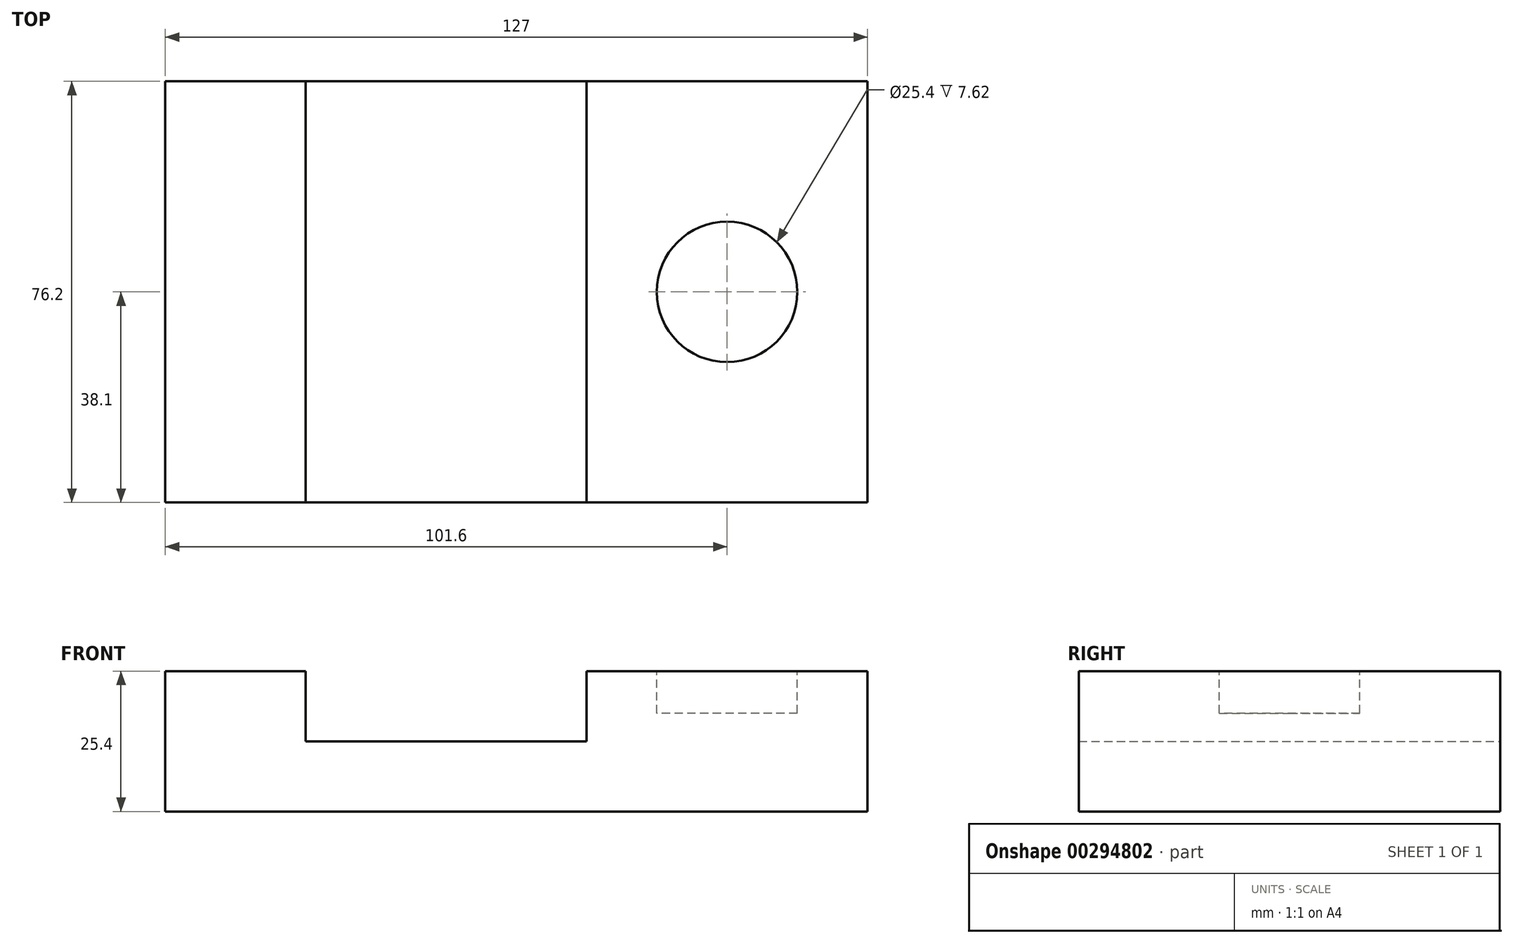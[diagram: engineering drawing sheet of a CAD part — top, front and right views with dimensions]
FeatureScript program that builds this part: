
annotation { "Feature Type Name" : "Feature", "Feature Type Description" : "" }
export const myFeature = defineFeature(function(context is Context, id is Id, definition is map)
    precondition{}
    {
        {
            var Q0;
            Q0=qCreatedBy(makeId("Top.planeOp"),FACE);
            var sketch = newSketch(context, id + "F0", { "sketchPlane" : qUnion([Q0])});
            skLineSegment(sketch, "E0.bottom", {"start": v(0, 0) * mm, "end": v(127, 0) * mm});
            skLineSegment(sketch, "E0.top", {"start": v(0, -76.2) * mm, "end": v(127, -76.2) * mm});
            skLineSegment(sketch, "E0.left", {"start": v(0, 0) * mm, "end": v(0, -76.2) * mm});
            skLineSegment(sketch, "E0.right", {"start": v(127, 0) * mm, "end": v(127, -76.2) * mm});
            skSolve(sketch);
        }
        {
            var Q0;
            Q0=makeQuery(id+"F0.imprint","IMPRINT",FACE,{"disambiguationData":[TD([[makeQuery(id+"F0.imprint","IMPRINT",EDGE,{"derivedFrom":sQuery(id+"F0.wireOp",EDGE,"E0.bottom")}),-1.0]])]});
            extrude(context, id + "F1", {"entities" : qUnion([Q0]), "depth" : 25.4 * mm});
        }
        {
            var Q0;
            Q0=makeQuery(id+"F1.opExtrude","CAP_FACE",FACE,{"disambiguationData":[OSD([sQuery(id+"F0.wireOp",EDGE,"E0.bottom"),sQuery(id+"F0.wireOp",EDGE,"E0.top"),sQuery(id+"F0.wireOp",EDGE,"E0.left"),sQuery(id+"F0.wireOp",EDGE,"E0.right")])],"isStart":false});
            var sketch = newSketch(context, id + "F2", { "sketchPlane" : qUnion([Q0])});
            skLineSegment(sketch, "E1.bottom", {"start": v(25.4, -76.2) * mm, "end": v(76.2, -76.2) * mm});
            skLineSegment(sketch, "E1.top", {"start": v(25.4, 0) * mm, "end": v(76.2, 0) * mm});
            skLineSegment(sketch, "E1.left", {"start": v(25.4, -76.2) * mm, "end": v(25.4, 0) * mm});
            skLineSegment(sketch, "E1.right", {"start": v(76.2, -76.2) * mm, "end": v(76.2, 0) * mm});
            skSolve(sketch);
        }
        {
            var Q0;
            Q0=makeQuery(id+"F2.imprint","IMPRINT",FACE,{"disambiguationData":[TD([[makeQuery(id+"F2.imprint","IMPRINT",EDGE,{"derivedFrom":sQuery(id+"F2.wireOp",EDGE,"E1.bottom")}),1.0]])]});
            extrude(context, id + "F3", {"entities" : qUnion([Q0]), "operationType" : NewBodyOperationType.REMOVE, "oppositeDirection" : true, "depth" : 12.7 * mm});
        }
        {
            var Q0;
            {var subQ0=sQuery(id+"F0.wireOp",EDGE,"E0.bottom");var subQ1=sQuery(id+"F0.wireOp",EDGE,"E0.right");var subQ2=sQuery(id+"F0.wireOp",EDGE,"E0.top");Q0=makeQuery(id+"F3.boolean.opBoolean","SPLIT",FACE,{"disambiguationData":[TD([makeQuery(id+"F1.opExtrude","SWEPT_FACE",FACE,{"disambiguationData":[OSD([subQ1])]})])],"derivedFrom":makeQuery(id+"F1.opExtrude","CAP_FACE",FACE,{"disambiguationData":[OSD([subQ0,subQ2,sQuery(id+"F0.wireOp",EDGE,"E0.left"),subQ1])],"isStart":false})});}
            var sketch = newSketch(context, id + "F4", { "sketchPlane" : qUnion([Q0])});
            skCircle(sketch, "E2", {"center": v(101.6, -38.1) * mm, "radius": 12.7 * mm});
            skSolve(sketch);
        }
        {
            var Q0;
            Q0 = qSketchRegion(id + "F4", true);
            extrude(context, id + "F5", {"entities" : qUnion([Q0]), "operationType" : NewBodyOperationType.REMOVE, "oppositeDirection" : true, "depth" : 7.62 * mm});
        }
    });
